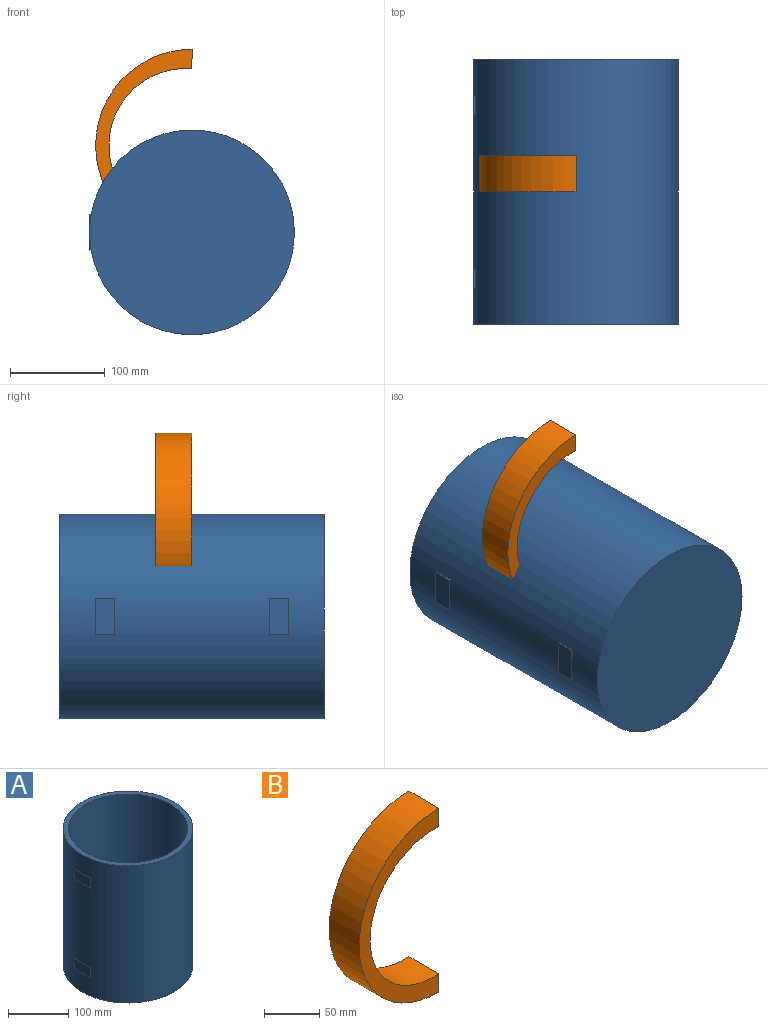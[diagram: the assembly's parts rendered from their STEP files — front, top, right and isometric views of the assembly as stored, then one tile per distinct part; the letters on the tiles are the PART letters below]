
ASSEMBLY  parts=2 mates=1
PART A: 20 faces, bbox 215.9x215.9x279.4 mm
  f0: plane 19.05x1.69mm, normal (0,0,-1), area 10.7mm2, adj f2,f4,f14
  f1: plane 19.05x1.69mm, normal (0,0,1), area 10.7mm2, adj f2,f4,f14
  f2: plane 20.3x1.69mm, normal (0,-1,0), area 34.4mm2, adj f0,f1,f4,f14
  f3: plane 20.3x1.69mm, normal (0,1,0), area 34.4mm2, adj f4,f5,f6,f14
  f4: plane 38.1x20.3mm, normal (-1,0,0), area 773.6mm2, adj f0,f1,f2,f3,f5,f6
  f5: plane 19.05x1.69mm, normal (0,0,-1), area 10.7mm2, adj f3,f4,f14
  f6: plane 19.05x1.69mm, normal (0,0,1), area 10.7mm2, adj f3,f4,f14
  f7: plane 19.05x1.69mm, normal (0,0,-1), area 10.7mm2, adj f9,f11,f14
  f8: plane 19.05x1.69mm, normal (0,0,1), area 10.7mm2, adj f9,f11,f14
  f9: plane 20.3x1.69mm, normal (0,-1,0), area 34.4mm2, adj f7,f8,f11,f14
  f10: plane 20.3x1.69mm, normal (0,1,0), area 34.4mm2, adj f11,f12,f13,f14
  f11: plane 38.1x20.3mm, normal (-1,0,0), area 773.6mm2, adj f7,f8,f9,f10,f12,f13
  f12: plane 19.05x1.69mm, normal (0,0,-1), area 10.7mm2, adj f10,f11,f14
  f13: plane 19.05x1.69mm, normal (0,0,1), area 10.7mm2, adj f10,f11,f14
  f14: cylinder r=107.95mm len=279.4mm, axis (0,0,-1), area 187953.3mm2, adj f0,f1,f2,f3,f5,f6,f7,f8
  f15: cylinder r=99.06mm len=266.7mm, axis (0,0,-1), area 165997.4mm2, adj f16,f19
  f16: plane 215.9x215.9mm, normal (0,0,1), area 5781.5mm2, adj f14,f15
  f17: plane 215.9x215.9mm, normal (0,0,-1), area 36609.6mm2, adj f14
  f18: plane 193.04x193.04mm, normal (0,0,1), area 29267.4mm2, adj f19
  f19: torus R=96.52mm, axis (0,0,1), area 2460.2mm2, adj f15,f18
PART B: 6 faces, bbox 101.6x38.1x203.2 mm
  f0: cylinder r=101.6mm len=203.2mm, axis (0,1,0), area 12161mm2, adj f1,f3,f4,f5
  f1: plane 38.1x20.32mm, normal (1,0,0), area 774.2mm2, adj f0,f2,f4,f5
  f2: cylinder r=81.51mm len=163.02mm, axis (0,1,0), area 10223.1mm2, adj f1,f3,f4,f5
  f3: plane 38.1x20.32mm, normal (1,0,0), area 774.2mm2, adj f0,f2,f4,f5
  f4: plane 203.2x101.6mm, normal (0,-1,0), area 4781.7mm2, adj f0,f1,f2,f3
  f5: plane 203.2x101.6mm, normal (0,1,0), area 4781.7mm2, adj f0,f1,f2,f3
PLACE A rot(axis=(-1,0,0),90deg) t=(-107.95,-57.77,-59.69)mm
PLACE B t=(0,208.93,0)mm
MATE fastened A.f14 <-> B.f4  axis (0,-1,0) through (0,81.93,48.26)mm
